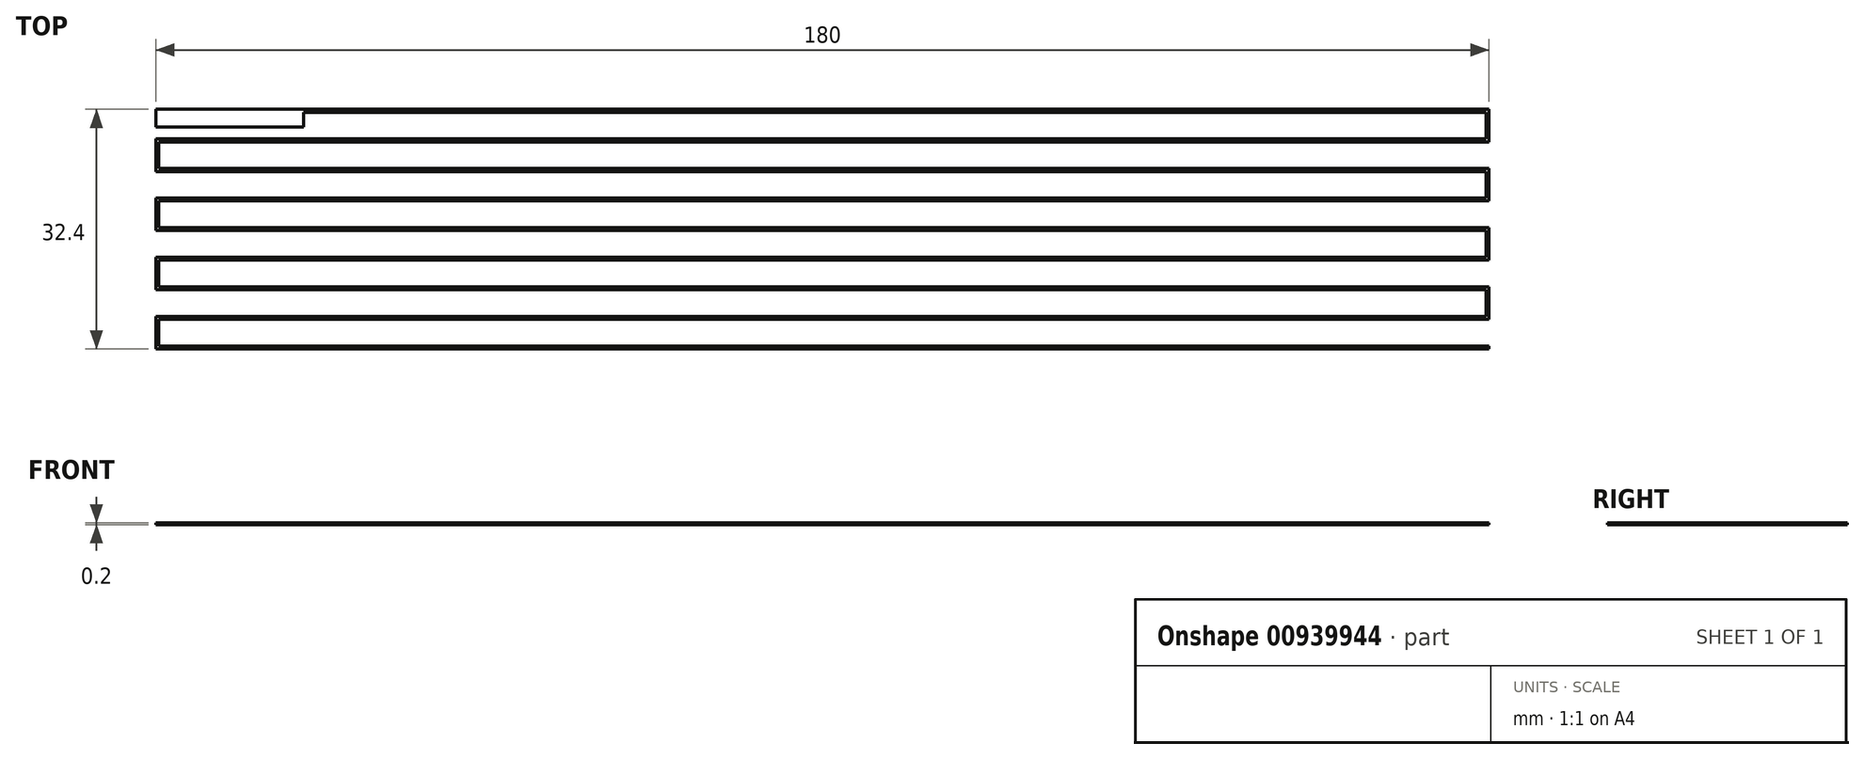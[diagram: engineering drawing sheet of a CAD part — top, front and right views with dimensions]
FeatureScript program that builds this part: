
annotation { "Feature Type Name" : "Feature", "Feature Type Description" : "" }
export const myFeature = defineFeature(function(context is Context, id is Id, definition is map)
    precondition{}
    {
        {
            var Q0;
            Q0=qCreatedBy(makeId("Top.planeOp"),FACE);
            var sketch = newSketch(context, id + "F0", { "sketchPlane" : qUnion([Q0])});
            skLineSegment(sketch, "E0", {"start": v(-53.72, 27.68) * mm, "end": v(125.88, 27.68) * mm});
            skLineSegment(sketch, "E1", {"start": v(125.88, 24.08) * mm, "end": v(-53.72, 24.08) * mm});
            skLineSegment(sketch, "E2", {"start": v(-53.72, 24.08) * mm, "end": v(-53.72, 19.68) * mm});
            skLineSegment(sketch, "E3", {"start": v(-53.72, 19.68) * mm, "end": v(125.88, 19.68) * mm});
            skLineSegment(sketch, "E4", {"start": v(125.88, 19.68) * mm, "end": v(125.88, 16.08) * mm});
            skLineSegment(sketch, "E5", {"start": v(125.88, 16.08) * mm, "end": v(-53.72, 16.08) * mm});
            skLineSegment(sketch, "E6", {"start": v(-53.72, 16.08) * mm, "end": v(-53.72, 11.68) * mm});
            skLineSegment(sketch, "E7", {"start": v(-53.72, 11.68) * mm, "end": v(125.88, 11.68) * mm});
            skLineSegment(sketch, "E8", {"start": v(126.28, 12.08) * mm, "end": v(-53.32, 12.08) * mm});
            skLineSegment(sketch, "E9", {"start": v(-53.32, 12.08) * mm, "end": v(-53.32, 15.68) * mm});
            skLineSegment(sketch, "E10", {"start": v(-53.32, 15.68) * mm, "end": v(126.28, 15.68) * mm});
            skLineSegment(sketch, "E11", {"start": v(126.28, 15.68) * mm, "end": v(126.28, 20.08) * mm});
            skLineSegment(sketch, "E12", {"start": v(126.28, 20.08) * mm, "end": v(-53.32, 20.08) * mm});
            skLineSegment(sketch, "E13", {"start": v(-53.32, 20.08) * mm, "end": v(-53.32, 23.68) * mm});
            skLineSegment(sketch, "E14", {"start": v(-53.32, 23.68) * mm, "end": v(126.28, 23.68) * mm});
            skLineSegment(sketch, "E15", {"start": v(126.28, 23.68) * mm, "end": v(126.28, 28.08) * mm});
            skLineSegment(sketch, "E16", {"start": v(126.28, 28.08) * mm, "end": v(-53.72, 28.08) * mm});
            skLineSegment(sketch, "E17", {"start": v(-53.72, 28.08) * mm, "end": v(-53.72, 27.68) * mm});
            skLineSegment(sketch, "E18", {"start": v(125.88, 27.68) * mm, "end": v(125.88, 24.08) * mm});
            skLineSegment(sketch, "E19", {"start": v(125.88, 8.08) * mm, "end": v(-53.72, 8.08) * mm});
            skLineSegment(sketch, "E20", {"start": v(-53.72, 8.08) * mm, "end": v(-53.72, 3.68) * mm});
            skLineSegment(sketch, "E21", {"start": v(-53.72, 3.68) * mm, "end": v(125.88, 3.68) * mm});
            skLineSegment(sketch, "E22", {"start": v(125.88, 3.68) * mm, "end": v(125.88, 0.08) * mm});
            skLineSegment(sketch, "E23", {"start": v(125.88, 0.08) * mm, "end": v(-53.72, 0.08) * mm});
            skLineSegment(sketch, "E24", {"start": v(-53.72, 0.08) * mm, "end": v(-53.72, -4.32) * mm});
            skLineSegment(sketch, "E25", {"start": v(-53.72, -4.32) * mm, "end": v(126.28, -4.32) * mm});
            skLineSegment(sketch, "E26", {"start": v(126.28, -4.32) * mm, "end": v(126.28, -3.92) * mm});
            skLineSegment(sketch, "E27", {"start": v(126.28, -3.92) * mm, "end": v(-53.32, -3.92) * mm});
            skLineSegment(sketch, "E28", {"start": v(-53.32, -3.92) * mm, "end": v(-53.32, -0.32) * mm});
            skLineSegment(sketch, "E29", {"start": v(-53.32, -0.32) * mm, "end": v(126.28, -0.32) * mm});
            skLineSegment(sketch, "E30", {"start": v(126.28, -0.32) * mm, "end": v(126.28, 4.08) * mm});
            skLineSegment(sketch, "E31", {"start": v(126.28, 4.08) * mm, "end": v(-53.32, 4.08) * mm});
            skLineSegment(sketch, "E32", {"start": v(-53.32, 4.08) * mm, "end": v(-53.32, 7.68) * mm});
            skLineSegment(sketch, "E33", {"start": v(-53.32, 7.68) * mm, "end": v(126.28, 7.68) * mm});
            skLineSegment(sketch, "E34", {"start": v(126.28, 12.08) * mm, "end": v(126.28, 7.68) * mm});
            skLineSegment(sketch, "E35", {"start": v(125.88, 11.68) * mm, "end": v(125.88, 8.08) * mm});
            skLineSegment(sketch, "E36.bottom", {"start": v(-53.72, 28.08) * mm, "end": v(-53.72, 28.08) * mm});
            skLineSegment(sketch, "E36.top", {"start": v(-53.72, 32.08) * mm, "end": v(-53.72, 32.08) * mm});
            skLineSegment(sketch, "E36.left", {"start": v(-53.72, 28.08) * mm, "end": v(-53.72, 32.08) * mm});
            skLineSegment(sketch, "E36.right", {"start": v(-53.72, 28.08) * mm, "end": v(-53.72, 32.08) * mm});
            skLineSegment(sketch, "E37", {"start": v(-53.72, 32.08) * mm, "end": v(-33.72, 32.08) * mm});
            skLineSegment(sketch, "E38", {"start": v(-33.72, 25.68) * mm, "end": v(-53.72, 25.68) * mm});
            skLineSegment(sketch, "E39", {"start": v(-53.72, 25.68) * mm, "end": v(-53.72, 27.68) * mm});
            skLineSegment(sketch, "E40", {"start": v(-33.72, 32.08) * mm, "end": v(-33.72, 25.68) * mm});
            skSolve(sketch);
        }
        {
            var Q0;
            Q0=makeQuery(id+"F0.imprint","IMPRINT",FACE,{"disambiguationData":[TD([[makeQuery(id+"F0.imprint","IMPRINT",EDGE,{"derivedFrom":sQuery(id+"F0.wireOp",EDGE,"E0")}),1.0]])]});
            var Q1;
            Q1=makeQuery(id+"F0.imprint","IMPRINT",FACE,{"disambiguationData":[TD([[makeQuery(id+"F0.imprint","IMPRINT",EDGE,{"derivedFrom":sQuery(id+"F0.wireOp",EDGE,"E38")}),-1.0]])]});
            var Q2;
            {var subQ0=sQuery(id+"F0.wireOp",EDGE,"E36.right");Q2=makeQuery(id+"F0.imprint","IMPRINT",FACE,{"disambiguationData":[TD([[makeQuery(id+"F0.imprint","IMPRINT",EDGE,{"derivedFrom":subQ0}),-1.0]])]});}
            var Q3;
            Q3=makeQuery(id+"F0.imprint","IMPRINT",FACE,{"disambiguationData":[TD([[makeQuery(id+"F0.imprint","IMPRINT",EDGE,{"derivedFrom":sQuery(id+"F0.wireOp",EDGE,"E1")}),1.0]])]});
            extrude(context, id + "F1", {"entities" : qUnion([Q0, Q1, Q2, Q3]), "depth" : 0.2 * mm, "offsetDistance" : 25 * mm});
        }
    });
